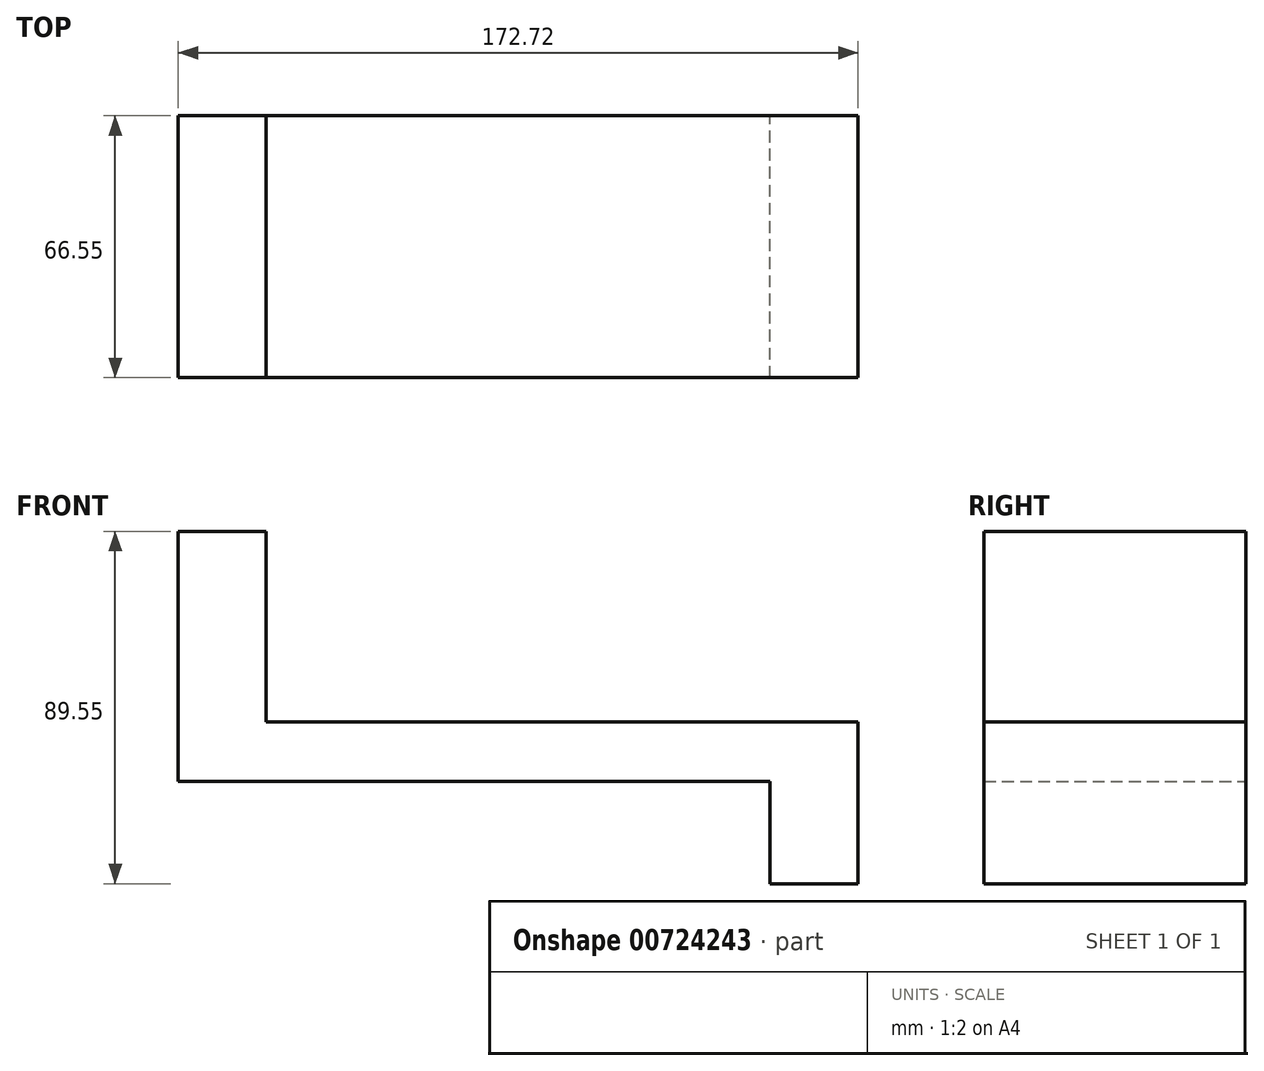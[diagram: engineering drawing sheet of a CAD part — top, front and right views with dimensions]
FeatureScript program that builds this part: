
annotation { "Feature Type Name" : "Feature", "Feature Type Description" : "" }
export const myFeature = defineFeature(function(context is Context, id is Id, definition is map)
    precondition{}
    {
        {
            var Q0;
            Q0=qCreatedBy(makeId("Front.planeOp"),FACE);
            var sketch = newSketch(context, id + "F0", { "sketchPlane" : qUnion([Q0])});
            skLineSegment(sketch, "E0", {"start": v(-58.26, 14.3) * mm, "end": v(-58.26, -49.2) * mm});
            skLineSegment(sketch, "E1", {"start": v(-58.26, -49.2) * mm, "end": v(92.1, -49.2) * mm});
            skLineSegment(sketch, "E2", {"start": v(92.1, -75.17) * mm, "end": v(92.1, -49.2) * mm});
            skLineSegment(sketch, "E3", {"start": v(92.1, -75.17) * mm, "end": v(114.46, -75.17) * mm});
            skLineSegment(sketch, "E4", {"start": v(114.46, -75.17) * mm, "end": v(114.46, -34.02) * mm});
            skLineSegment(sketch, "E5", {"start": v(114.46, -34.02) * mm, "end": v(-35.91, -34.02) * mm});
            skLineSegment(sketch, "E6", {"start": v(-35.91, -34.02) * mm, "end": v(-35.91, 14.38) * mm});
            skLineSegment(sketch, "E7", {"start": v(-58.26, 14.3) * mm, "end": v(-35.91, 14.38) * mm});
            skSolve(sketch);
        }
        {
            var Q0;
            Q0=makeQuery(id+"F0.imprint","IMPRINT",FACE,{"disambiguationData":[TD([[makeQuery(id+"F0.imprint","IMPRINT",EDGE,{"derivedFrom":sQuery(id+"F0.wireOp",EDGE,"E0")}),1.0]])]});
            extrude(context, id + "F1", {"entities" : qUnion([Q0]), "depth" : 66.55 * mm, "offsetDistance" : 25.4 * mm});
        }
    });
